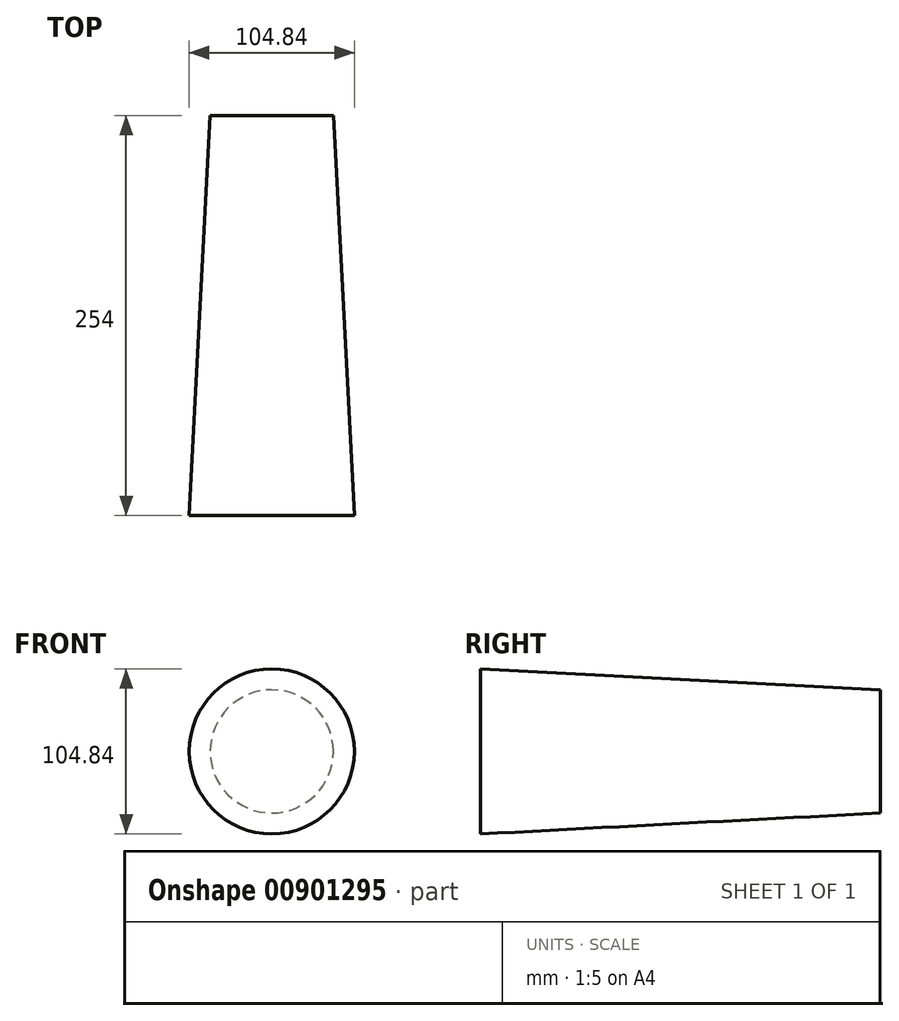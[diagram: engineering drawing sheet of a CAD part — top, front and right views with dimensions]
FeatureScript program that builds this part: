
annotation { "Feature Type Name" : "Feature", "Feature Type Description" : "" }
export const myFeature = defineFeature(function(context is Context, id is Id, definition is map)
    precondition{}
    {
        {
            var Q0;
            Q0=qCreatedBy(makeId("Front.planeOp"),FACE);
            var sketch = newSketch(context, id + "F0", { "sketchPlane" : qUnion([Q0])});
            skCircle(sketch, "E0", {"center": v(0, -17.55) * mm, "radius": 39.1 * mm});
            skSolve(sketch);
        }
        {
            var Q0;
            Q0=makeQuery(id+"F0.imprint","IMPRINT",FACE,{"disambiguationData":[TD([[makeQuery(id+"F0.imprint","IMPRINT",EDGE,{"derivedFrom":sQuery(id+"F0.wireOp",EDGE,"E0")}),1.0]])]});
            extrude(context, id + "F1", {"entities" : qUnion([Q0]), "depth" : 254 * mm, "offsetDistance" : 25.4 * mm, "hasDraft" : true, "draftAngle" : 3 * degree});
        }
    });
